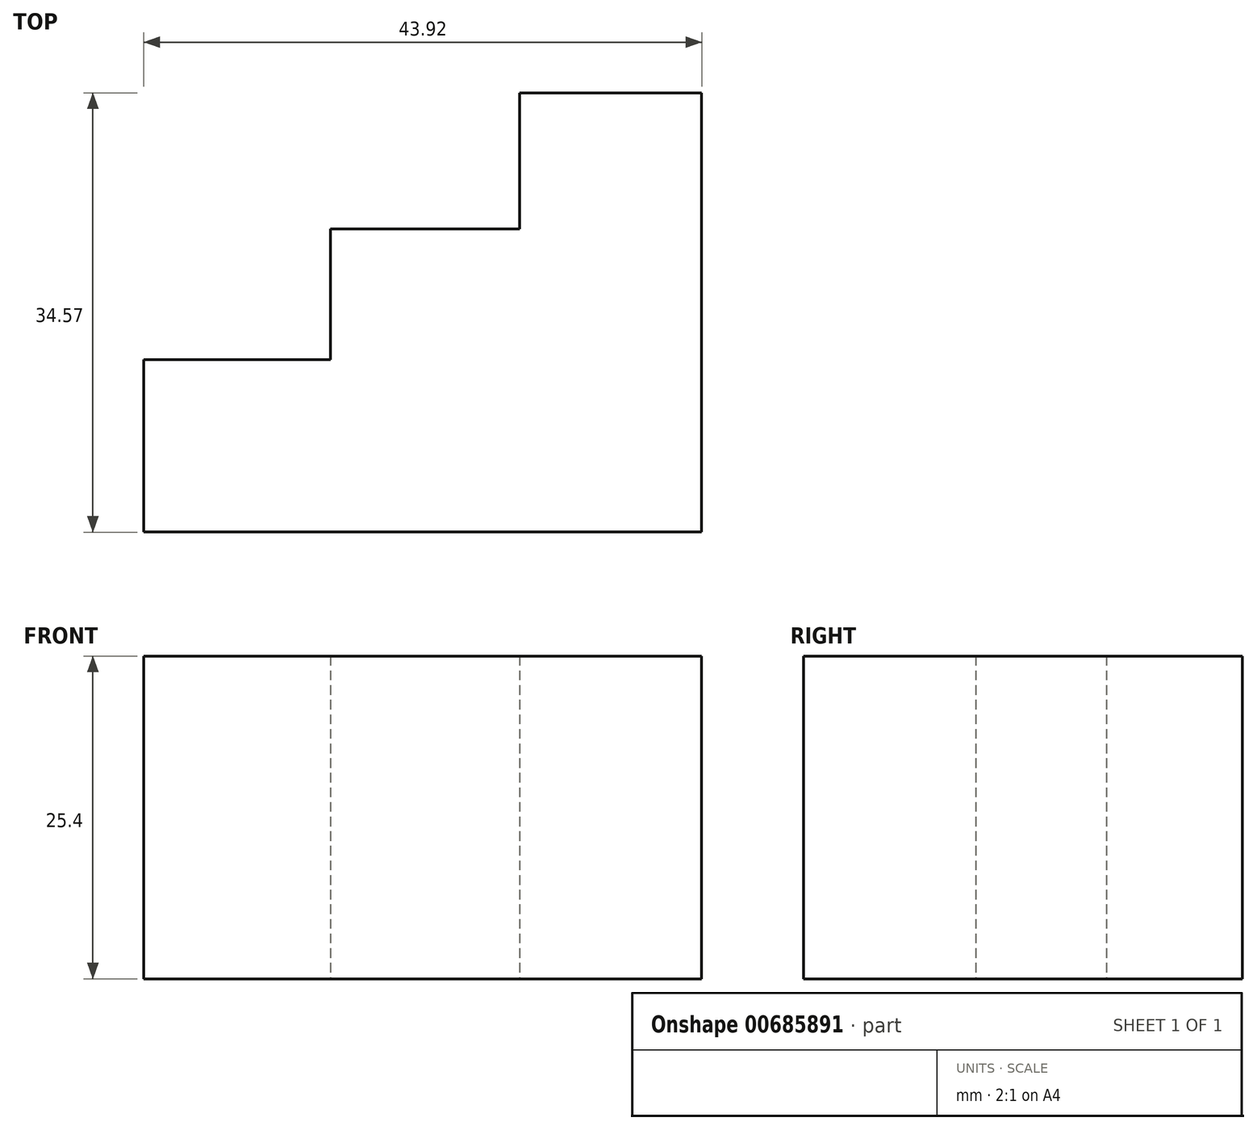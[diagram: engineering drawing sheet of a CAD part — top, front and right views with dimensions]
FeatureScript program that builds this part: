
annotation { "Feature Type Name" : "Feature", "Feature Type Description" : "" }
export const myFeature = defineFeature(function(context is Context, id is Id, definition is map)
    precondition{}
    {
        {
            var Q0;
            Q0=qCreatedBy(makeId("Top.planeOp"),FACE);
            var sketch = newSketch(context, id + "F0", { "sketchPlane" : qUnion([Q0])});
            skLineSegment(sketch, "E0.bottom", {"start": v(-33.13, 9.07) * mm, "end": v(-18.43, 9.07) * mm});
            skLineSegment(sketch, "E0.top", {"start": v(-33.13, -4.49) * mm, "end": v(-18.43, -4.49) * mm});
            skLineSegment(sketch, "E0.left", {"start": v(-33.13, 9.07) * mm, "end": v(-33.13, -4.49) * mm});
            skPoint(sketch, "E1.oppositeSnap0", {"position": v(-18.43, 2.3) * mm});
            skLineSegment(sketch, "E1.bottom", {"start": v(-3.53, -4.49) * mm, "end": v(-18.43, -4.49) * mm});
            skLineSegment(sketch, "E1.top", {"start": v(-3.53, 19.38) * mm, "end": v(-18.43, 19.38) * mm});
            skLineSegment(sketch, "E1.right", {"start": v(-18.43, 9.07) * mm, "end": v(-18.43, 19.38) * mm});
            skLineSegment(sketch, "E2.bottom", {"start": v(10.79, -4.49) * mm, "end": v(-3.53, -4.49) * mm});
            skLineSegment(sketch, "E2.top", {"start": v(10.79, 30.08) * mm, "end": v(-3.53, 30.08) * mm});
            skLineSegment(sketch, "E2.left", {"start": v(10.79, -4.49) * mm, "end": v(10.79, 30.08) * mm});
            skLineSegment(sketch, "E2.right", {"start": v(-3.53, 19.38) * mm, "end": v(-3.53, 30.08) * mm});
            skSolve(sketch);
        }
        {
            var Q0;
            Q0 = qSketchRegion(id + "F0", true);
            extrude(context, id + "F1", {"entities" : qUnion([Q0]), "depth" : 25.4 * mm, "offsetDistance" : 25.4 * mm});
        }
    });
